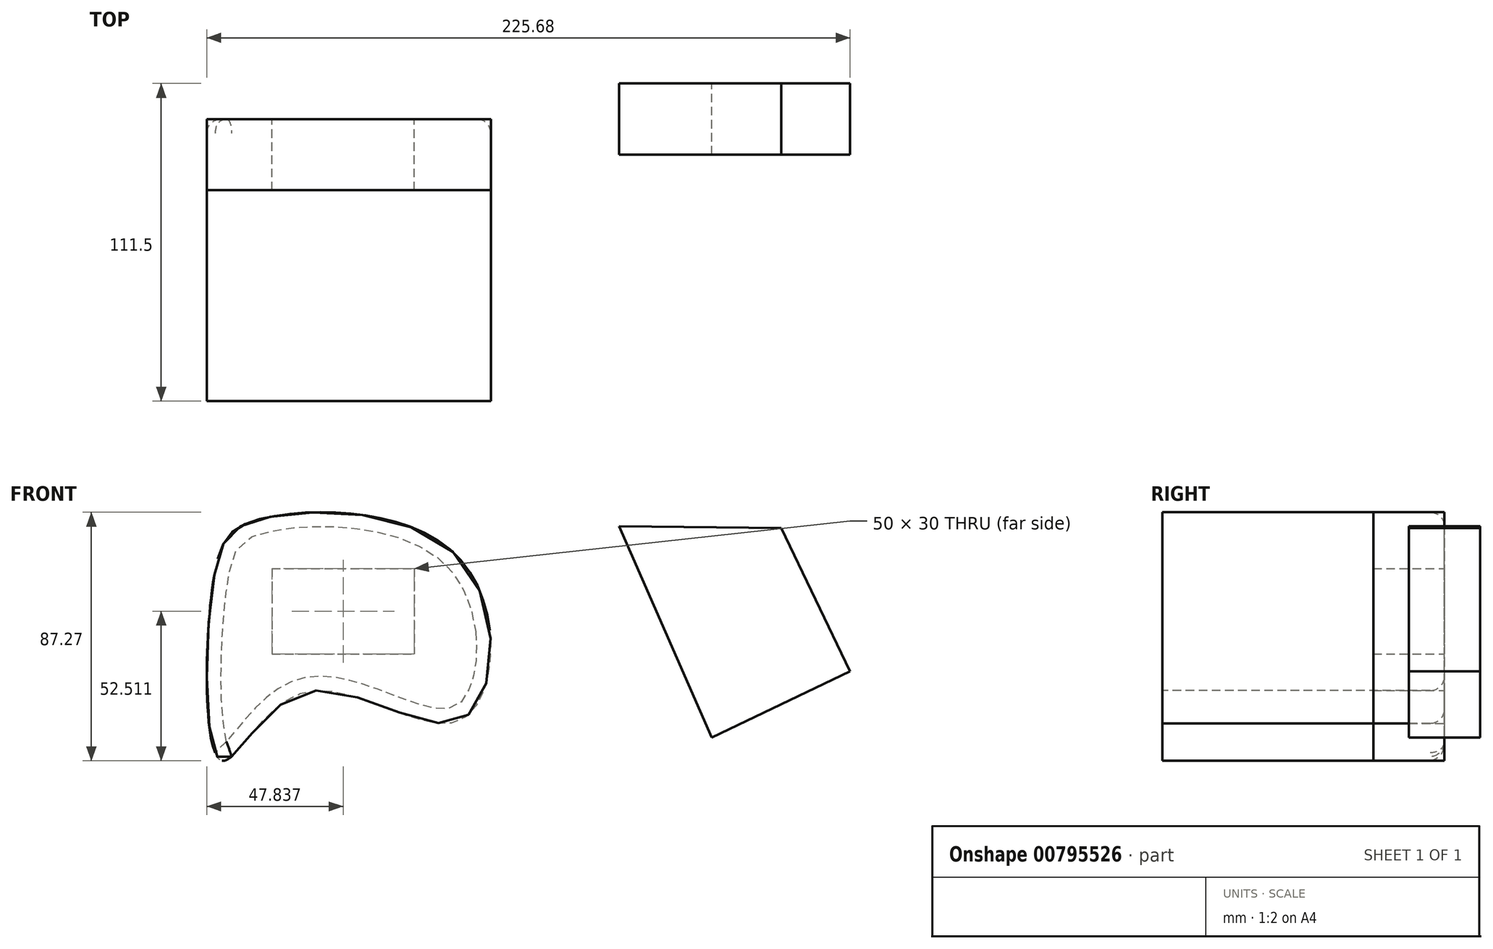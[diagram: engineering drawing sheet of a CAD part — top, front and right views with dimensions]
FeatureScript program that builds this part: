
annotation { "Feature Type Name" : "Feature", "Feature Type Description" : "" }
export const myFeature = defineFeature(function(context is Context, id is Id, definition is map)
    precondition{}
    {
        {
            var Q0;
            Q0=qCreatedBy(makeId("Front.planeOp"),FACE);
            var sketch = newSketch(context, id + "F0", { "sketchPlane" : qUnion([Q0])});
            skFitSpline(sketch, "E0", {"points": [v(-122.59, 33.94) * mm, v(-106.63, 53.45) * mm, v(-35.35, 38.2) * mm, v(-36.42, -17.12) * mm, v(-91.74, -7.54) * mm, v(-120.1, -31.3) * mm, v(-122.59, 33.94) * mm]});
            skLineSegment(sketch, "E1.bottom", {"start": v(-102.42, 36.11) * mm, "end": v(-52.42, 36.11) * mm});
            skLineSegment(sketch, "E1.top", {"start": v(-102.42, 6.11) * mm, "end": v(-52.42, 6.11) * mm});
            skLineSegment(sketch, "E1.left", {"start": v(-102.42, 36.11) * mm, "end": v(-102.42, 6.11) * mm});
            skLineSegment(sketch, "E1.right", {"start": v(-52.42, 36.11) * mm, "end": v(-52.42, 6.11) * mm});
            skLineSegment(sketch, "E2", {"start": v(19.46, 51) * mm, "end": v(76.34, 50.25) * mm});
            skLineSegment(sketch, "E3", {"start": v(76.34, 50.25) * mm, "end": v(100.42, 0) * mm});
            skLineSegment(sketch, "E4", {"start": v(100.42, 0) * mm, "end": v(51.95, -23.22) * mm});
            skLineSegment(sketch, "E5", {"start": v(51.95, -23.22) * mm, "end": v(19.46, 51) * mm});
            skSolve(sketch);
        }
        {
            var Q0;
            Q0=makeQuery(id+"F0.imprint","IMPRINT",FACE,{"disambiguationData":[TD([[makeQuery(id+"F0.imprint","IMPRINT",EDGE,{"derivedFrom":sQuery(id+"F0.wireOp",EDGE,"E2")}),-1.0]])]});
            extrude(context, id + "F1", {"entities" : qUnion([Q0]), "endBound" : BoundingType.SYMMETRIC, "depth" : 25 * mm, "offsetDistance" : 25 * mm});
        }
        {
            var Q0;
            Q0=makeQuery(id+"F0.imprint","IMPRINT",FACE,{"disambiguationData":[TD([[makeQuery(id+"F0.imprint","IMPRINT",EDGE,{"derivedFrom":sQuery(id+"F0.wireOp",EDGE,"E0")}),-1.0]])]});
            var Q1;
            Q1=makeQuery(id+"F0.imprint","IMPRINT",FACE,{"disambiguationData":[TD([[makeQuery(id+"F0.imprint","IMPRINT",EDGE,{"derivedFrom":sQuery(id+"F0.wireOp",EDGE,"E1.bottom")}),-1.0]])]});
            extrude(context, id + "F2", {"entities" : qUnion([Q0, Q1]), "depth" : 99 * mm, "offsetDistance" : 25 * mm});
        }
        {
            var Q0;
            Q0=makeQuery(id+"F2.opExtrude","CAP_EDGE",EDGE,{"disambiguationData":[OSD([sQuery(id+"F0.wireOp",EDGE,"E0")])],"isStart":true});
            fillet(context, id + "F3", {"entities" : qUnion([Q0]), "radius" : 5 * mm, "tangentPropagation" : true, "allowEdgeOverflow" : false});
        }
        {
            var Q0;
            Q0=makeQuery(id+"F0.imprint","IMPRINT",FACE,{"disambiguationData":[TD([[makeQuery(id+"F0.imprint","IMPRINT",EDGE,{"derivedFrom":sQuery(id+"F0.wireOp",EDGE,"E0")}),-1.0]])]});
            var Q1;
            Q1=makeQuery(id+"F1.opExtrude","CAP_FACE",FACE,{"disambiguationData":[OSD([sQuery(id+"F0.wireOp",EDGE,"E2"),sQuery(id+"F0.wireOp",EDGE,"E3"),sQuery(id+"F0.wireOp",EDGE,"E4"),sQuery(id+"F0.wireOp",EDGE,"E5")])],"isStart":true});
            extrude(context, id + "F4", {"entities" : qUnion([Q0, Q1]), "depth" : 25 * mm, "offsetDistance" : 25 * mm});
        }
    });
